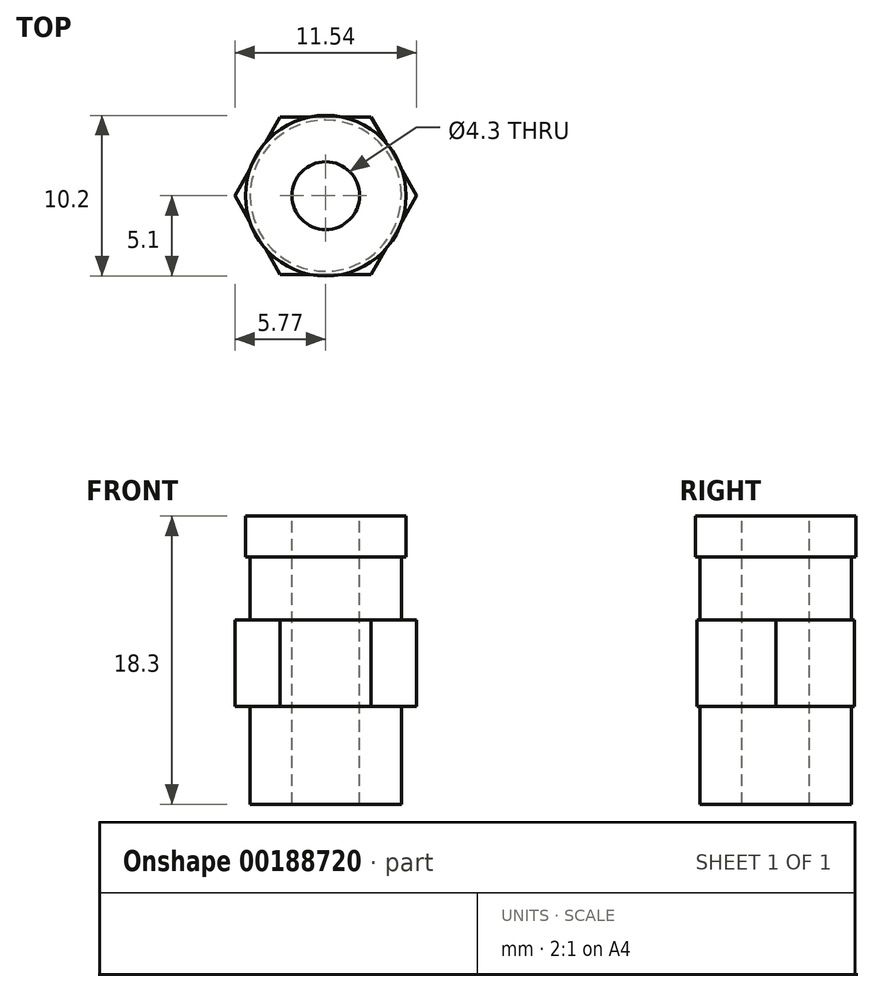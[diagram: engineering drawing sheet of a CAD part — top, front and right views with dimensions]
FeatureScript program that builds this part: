
annotation { "Feature Type Name" : "Feature", "Feature Type Description" : "" }
export const myFeature = defineFeature(function(context is Context, id is Id, definition is map)
    precondition{}
    {
        {
            var Q0;
            Q0=qCreatedBy(makeId("Top.planeOp"),FACE);
            var sketch = newSketch(context, id + "F0", { "sketchPlane" : qUnion([Q0])});
            skCircle(sketch, "E0", {"center": v(0, 0) * mm, "radius": 4.8 * mm});
            skSolve(sketch);
        }
        {
            var Q0;
            Q0=makeQuery(id+"F0.imprint","IMPRINT",FACE,{"disambiguationData":[TD([[makeQuery(id+"F0.imprint","IMPRINT",EDGE,{"derivedFrom":sQuery(id+"F0.wireOp",EDGE,"E0")}),1.0]])]});
            extrude(context, id + "F1", {"entities" : qUnion([Q0]), "depth" : 6.2 * mm});
        }
        {
            var Q0;
            Q0=makeQuery(id+"F1.opExtrude","CAP_FACE",FACE,{"disambiguationData":[OSD([sQuery(id+"F0.wireOp",EDGE,"E0")])],"isStart":false});
            var sketch = newSketch(context, id + "F2", { "sketchPlane" : qUnion([Q0])});
            skCircle(sketch, "E1.cCircle", {"center": v(0, 0) * mm, "radius": 5 * mm, "construction": true});
            skLineSegment(sketch, "E1.0", {"start": v(5.77, 0) * mm, "end": v(2.89, -5) * mm});
            skLineSegment(sketch, "E1.1", {"start": v(2.89, -5) * mm, "end": v(-2.89, -5) * mm});
            skLineSegment(sketch, "E1.2", {"start": v(-2.89, -5) * mm, "end": v(-5.77, 0) * mm});
            skLineSegment(sketch, "E1.3", {"start": v(-5.77, 0) * mm, "end": v(-2.89, 5) * mm});
            skLineSegment(sketch, "E1.4", {"start": v(-2.89, 5) * mm, "end": v(2.89, 5) * mm});
            skLineSegment(sketch, "E1.5", {"start": v(2.89, 5) * mm, "end": v(5.77, 0) * mm});
            skPoint(sketch, "E1.0.midPoint", {"position": v(4.33, -2.5) * mm});
            skSolve(sketch);
        }
        {
            var Q0;
            Q0=makeQuery(id+"F2.imprint","IMPRINT",FACE,{"disambiguationData":[TD([[makeQuery(id+"F2.imprint","IMPRINT",EDGE,{"derivedFrom":sQuery(id+"F2.wireOp",EDGE,"E1.0")}),-1.0]])]});
            var Q1;
            Q1=makeQuery(id+"F2.imprint","IMPRINT",FACE,{"disambiguationData":[TD([[makeQuery(id+"F2.imprint","IMPRINT",EDGE,{"derivedFrom":makeQuery(id+"F1.opExtrude","CAP_EDGE",EDGE,{"disambiguationData":[OSD([sQuery(id+"F0.wireOp",EDGE,"E0")])],"isStart":false})}),1.0]])]});
            extrude(context, id + "F3", {"entities" : qUnion([Q0, Q1]), "operationType" : NewBodyOperationType.ADD, "depth" : 5.5 * mm});
        }
        {
            var Q0;
            Q0=makeQuery(id+"F3.opExtrude","CAP_FACE",FACE,{"disambiguationData":[OSD([sQuery(id+"F2.wireOp",EDGE,"E1.0"),sQuery(id+"F2.wireOp",EDGE,"E1.1"),sQuery(id+"F2.wireOp",EDGE,"E1.2"),sQuery(id+"F2.wireOp",EDGE,"E1.3"),sQuery(id+"F2.wireOp",EDGE,"E1.4"),sQuery(id+"F2.wireOp",EDGE,"E1.5")])],"isStart":false});
            var sketch = newSketch(context, id + "F4", { "sketchPlane" : qUnion([Q0])});
            skCircle(sketch, "E2", {"center": v(0, 0) * mm, "radius": 4.8 * mm});
            skSolve(sketch);
        }
        {
            var Q0;
            Q0=makeQuery(id+"F4.imprint","IMPRINT",FACE,{"disambiguationData":[TD([[makeQuery(id+"F4.imprint","IMPRINT",EDGE,{"derivedFrom":sQuery(id+"F4.wireOp",EDGE,"E2")}),1.0]])]});
            extrude(context, id + "F5", {"entities" : qUnion([Q0]), "operationType" : NewBodyOperationType.ADD, "depth" : 4 * mm});
        }
        {
            var Q0;
            Q0=makeQuery(id+"F5.opExtrude","CAP_FACE",FACE,{"disambiguationData":[OSD([sQuery(id+"F4.wireOp",EDGE,"E2")])],"isStart":false});
            var sketch = newSketch(context, id + "F6", { "sketchPlane" : qUnion([Q0])});
            skCircle(sketch, "E3", {"center": v(0, 0) * mm, "radius": 5.1 * mm});
            skSolve(sketch);
        }
        {
            var Q0;
            Q0=makeQuery(id+"F6.imprint","IMPRINT",FACE,{"disambiguationData":[TD([[makeQuery(id+"F6.imprint","IMPRINT",EDGE,{"derivedFrom":makeQuery(id+"F5.opExtrude","CAP_EDGE",EDGE,{"disambiguationData":[OSD([sQuery(id+"F4.wireOp",EDGE,"E2")])],"isStart":false})}),1.0]])]});
            var Q1;
            Q1=makeQuery(id+"F6.imprint","IMPRINT",FACE,{"disambiguationData":[TD([[makeQuery(id+"F6.imprint","IMPRINT",EDGE,{"derivedFrom":sQuery(id+"F6.wireOp",EDGE,"E3")}),1.0]])]});
            extrude(context, id + "F7", {"entities" : qUnion([Q0, Q1]), "operationType" : NewBodyOperationType.ADD, "depth" : (18.3 - 15.7) * mm});
        }
        {
            var Q0;
            Q0=makeQuery(id+"F7.opExtrude","CAP_FACE",FACE,{"disambiguationData":[OSD([sQuery(id+"F6.wireOp",EDGE,"E3")])],"isStart":false});
            var sketch = newSketch(context, id + "F8", { "sketchPlane" : qUnion([Q0])});
            skCircle(sketch, "E4", {"center": v(0, 0) * mm, "radius": 2.15 * mm});
            skSolve(sketch);
        }
        {
            var Q0;
            Q0=makeQuery(id+"F8.imprint","IMPRINT",FACE,{"disambiguationData":[TD([[makeQuery(id+"F8.imprint","IMPRINT",EDGE,{"derivedFrom":sQuery(id+"F8.wireOp",EDGE,"E4")}),1.0]])]});
            extrude(context, id + "F9", {"entities" : qUnion([Q0]), "operationType" : NewBodyOperationType.REMOVE, "endBound" : BoundingType.THROUGH_ALL, "oppositeDirection" : true, "depth" : 25 * mm});
        }
    });
